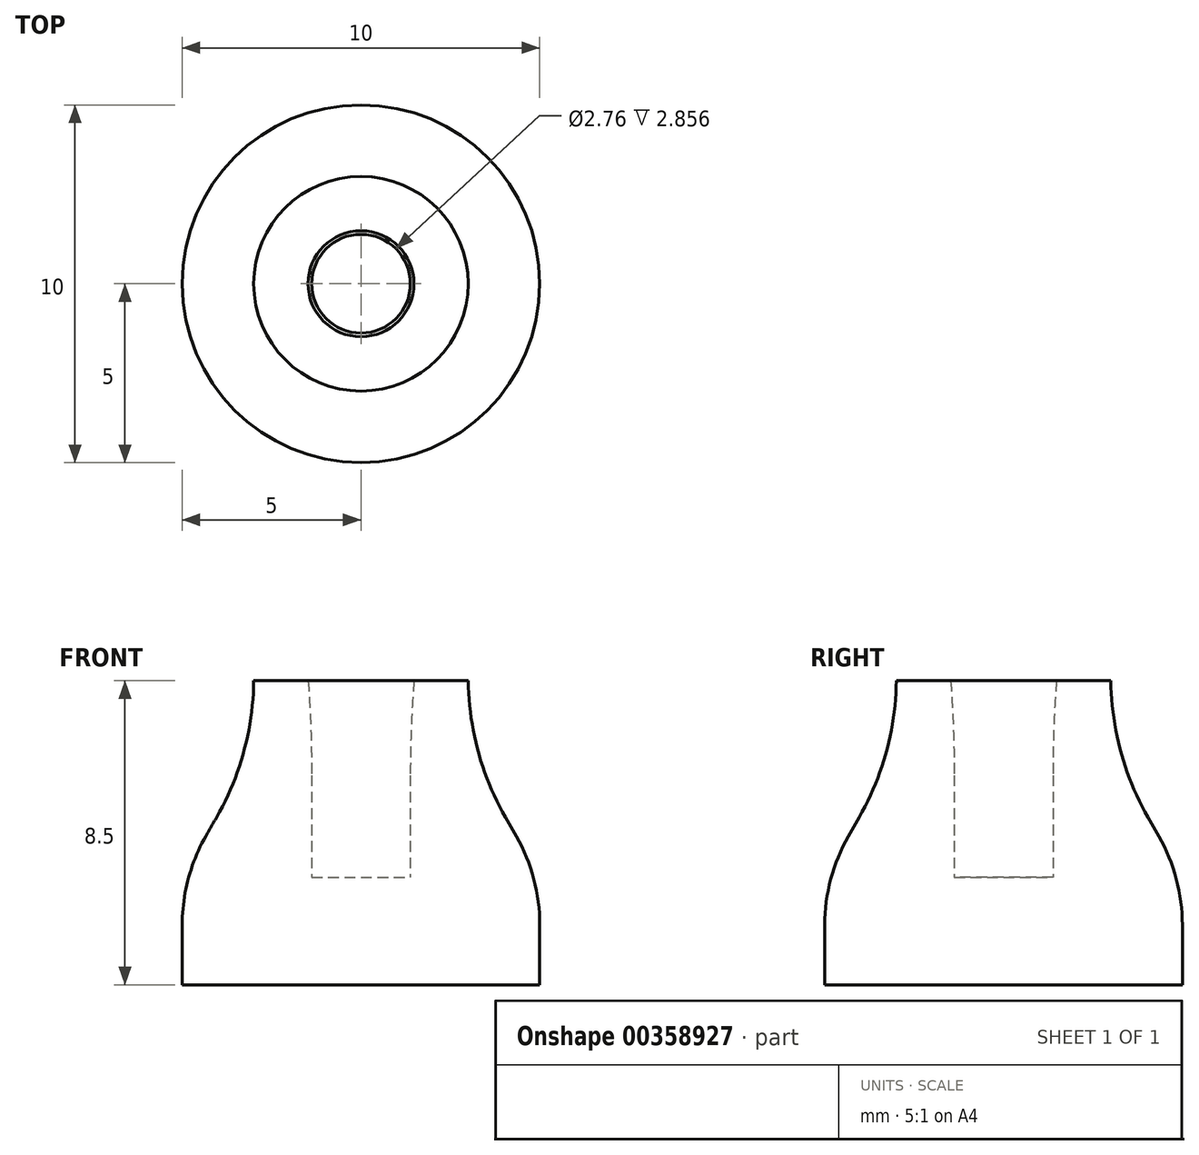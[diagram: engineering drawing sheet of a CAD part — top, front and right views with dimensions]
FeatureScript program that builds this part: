
annotation { "Feature Type Name" : "Feature", "Feature Type Description" : "" }
export const myFeature = defineFeature(function(context is Context, id is Id, definition is map)
    precondition{}
    {
        {
            var Q0;
            Q0=qCreatedBy(makeId("Front.planeOp"),FACE);
            var sketch = newSketch(context, id + "F0", { "sketchPlane" : qUnion([Q0])});
            skLineSegment(sketch, "E0", {"start": v(0, 0) * mm, "end": v(5, 0) * mm});
            skLineSegment(sketch, "E1", {"start": v(5, 3) * mm, "end": v(5, 0) * mm});
            skLineSegment(sketch, "E2", {"start": v(5, 3) * mm, "end": v(0, 3) * mm, "construction": true});
            skLineSegment(sketch, "E3", {"start": v(0, 3) * mm, "end": v(0, 6.5) * mm, "construction": true});
            skLineSegment(sketch, "E4", {"start": v(0, 6.5) * mm, "end": v(3, 6.5) * mm});
            skLineSegment(sketch, "E5", {"start": v(3, 6.5) * mm, "end": v(5, 3) * mm});
            skLineSegment(sketch, "E6.0", {"start": v(1.38, 3) * mm, "end": v(1.38, 6.5) * mm});
            skLineSegment(sketch, "E7", {"start": v(1.38, 3) * mm, "end": v(0, 3) * mm});
            skLineSegment(sketch, "E8", {"start": v(0, 3) * mm, "end": v(0, 0) * mm, "construction": true});
            skLineSegment(sketch, "E9", {"start": v(0, 3) * mm, "end": v(0, 0) * mm});
            skLineSegment(sketch, "E10", {"start": v(0, 3) * mm, "end": v(1.38, 3) * mm});
            skSolve(sketch);
        }
        {
            var Q0;
            Q0=makeQuery(id+"F0.imprint","IMPRINT",FACE,{"disambiguationData":[TD([[makeQuery(id+"F0.imprint","IMPRINT",EDGE,{"derivedFrom":sQuery(id+"F0.wireOp",EDGE,"E0")}),1.0]])]});
            var Q1;
            Q1=sQuery(id+"F0.wireOp",EDGE,"E3");
            revolve(context, id + "F1", {"entities" : qUnion([Q0]), "axis" : qUnion([Q1]), "revolveType" : RevolveType.FULL});
        }
        {
            var Q0;
            Q0=makeQuery(id+"F1.opRevolve","SWEPT_EDGE",EDGE,{"disambiguationData":[OSD([sQuery(id+"F0.wireOp",EDGE,"E1"),sQuery(id+"F0.wireOp",EDGE,"E5")])]});
            fillet(context, id + "F2", {"entities" : qUnion([Q0]), "radius" : 5 * mm, "tangentPropagation" : true, "allowEdgeOverflow" : false});
        }
        {
            var Q0;
            Q0=makeQuery(id+"F1.opRevolve","SWEPT_FACE",FACE,{"disambiguationData":[OSD([sQuery(id+"F0.wireOp",EDGE,"E4")])]});
            extrude(context, id + "F3", {"entities" : qUnion([Q0]), "operationType" : NewBodyOperationType.ADD, "depth" : 2 * mm, "offsetDistance" : 25 * mm});
        }
        {
            var Q0;
            Q0=makeQuery(id+"F3.opExtrude","CAP_EDGE",EDGE,{"disambiguationData":[OSD([sQuery(id+"F0.wireOp",EDGE,"E4"),sQuery(id+"F0.wireOp",EDGE,"E6.0")])],"isStart":false});
            chamfer(context, id + "F4", {"entities" : qUnion([Q0]), "width" : 0.1 * mm, "tangentPropagation" : true});
        }
        {
            var Q0;
            {var subQ0=sQuery(id+"F0.wireOp",EDGE,"E6.0");var subQ1=sQuery(id+"F0.wireOp",EDGE,"E4");Q0=makeQuery(id+"F4.opChamfer","BLEND_EDGE",EDGE,{"blendedFrom":[makeQuery(id+"F3.opExtrude","CAP_EDGE",EDGE,{"disambiguationData":[OSD([subQ1,subQ0])],"isStart":false}),makeQuery(id+"F3.boolean.opBoolean","MERGE",FACE,{"derivedFrom":[makeQuery(id+"F1.opRevolve","SWEPT_FACE",FACE,{"disambiguationData":[OSD([subQ0])]}),makeQuery(id+"F3.opExtrude","SWEPT_FACE",FACE,{"disambiguationData":[OSD([subQ1,subQ0])]})]})],"blendedInto":[makeQuery(id+"F3.boolean.opBoolean","MERGE",FACE,{"derivedFrom":[makeQuery(id+"F1.opRevolve","SWEPT_FACE",FACE,{"disambiguationData":[OSD([subQ0])]}),makeQuery(id+"F3.opExtrude","SWEPT_FACE",FACE,{"disambiguationData":[OSD([subQ1,subQ0])]})]})]});}
            fillet(context, id + "F5", {"entities" : qUnion([Q0]), "radius" : 35 * mm, "tangentPropagation" : true, "allowEdgeOverflow" : false});
        }
        {
            var Q0;
            {var subQ0=sQuery(id+"F0.wireOp",EDGE,"E5");var subQ1=sQuery(id+"F0.wireOp",EDGE,"E4");Q0=makeQuery(id+"F3.boolean.opBoolean","MERGE",EDGE,{"derivedFrom":[makeQuery(id+"F1.opRevolve","SWEPT_EDGE",EDGE,{"disambiguationData":[OSD([subQ1,subQ0])]}),makeQuery(id+"F3.opExtrude","CAP_EDGE",EDGE,{"disambiguationData":[OSD([subQ1,subQ0])],"isStart":true})]});}
            fillet(context, id + "F6", {"entities" : qUnion([Q0]), "radius" : 7.9 * mm, "tangentPropagation" : true, "allowEdgeOverflow" : false});
        }
    });
